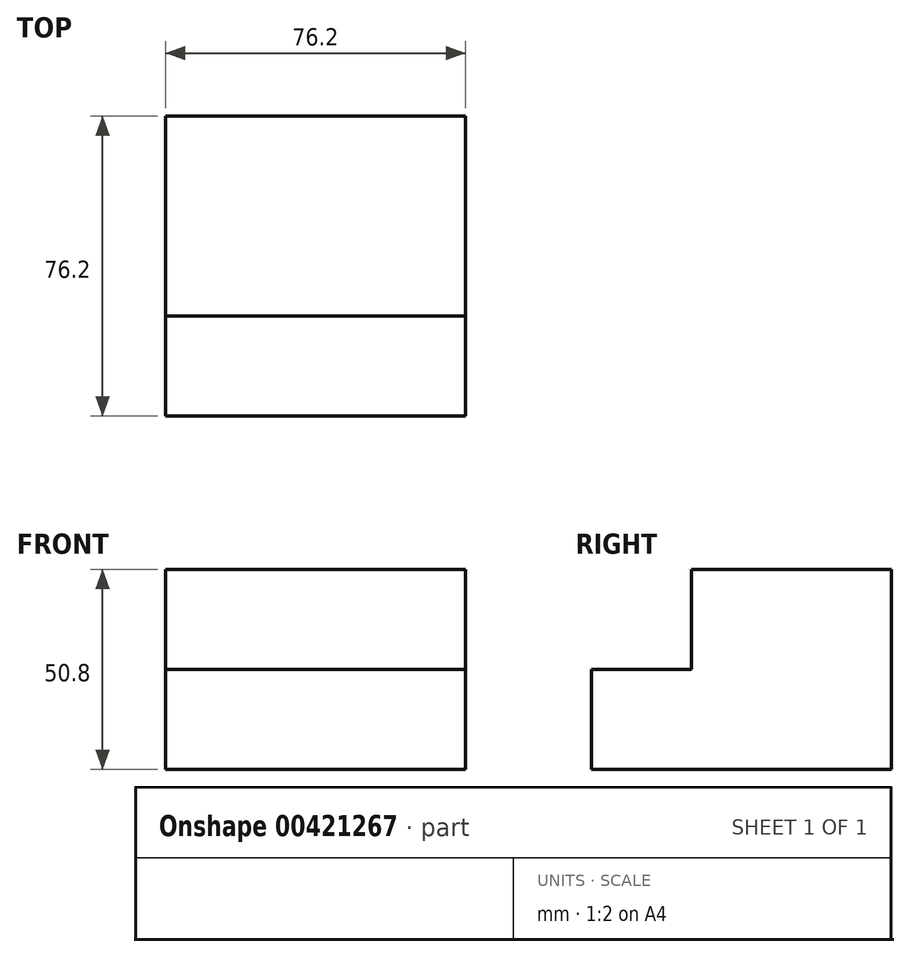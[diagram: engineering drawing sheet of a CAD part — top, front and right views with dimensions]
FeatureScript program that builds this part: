
annotation { "Feature Type Name" : "Feature", "Feature Type Description" : "" }
export const myFeature = defineFeature(function(context is Context, id is Id, definition is map)
    precondition{}
    {
        {
            var Q0;
            Q0=qCreatedBy(makeId("Right.planeOp"),FACE);
            var sketch = newSketch(context, id + "F0", { "sketchPlane" : qUnion([Q0])});
            skLineSegment(sketch, "E0", {"start": v(0, 0) * mm, "end": v(76.2, 0) * mm});
            skLineSegment(sketch, "E1", {"start": v(76.2, 0) * mm, "end": v(76.2, 50.8) * mm});
            skLineSegment(sketch, "E2", {"start": v(76.2, 50.8) * mm, "end": v(25.4, 50.8) * mm});
            skLineSegment(sketch, "E3", {"start": v(25.4, 50.8) * mm, "end": v(25.4, 25.4) * mm});
            skLineSegment(sketch, "E4", {"start": v(25.4, 25.4) * mm, "end": v(0, 25.4) * mm});
            skLineSegment(sketch, "E5", {"start": v(0, 25.4) * mm, "end": v(0, 0) * mm});
            skSolve(sketch);
        }
        {
            var Q0;
            Q0 = qSketchRegion(id + "F0", true);
            extrude(context, id + "F1", {"entities" : qUnion([Q0]), "depth" : 76.2 * mm});
        }
    });
